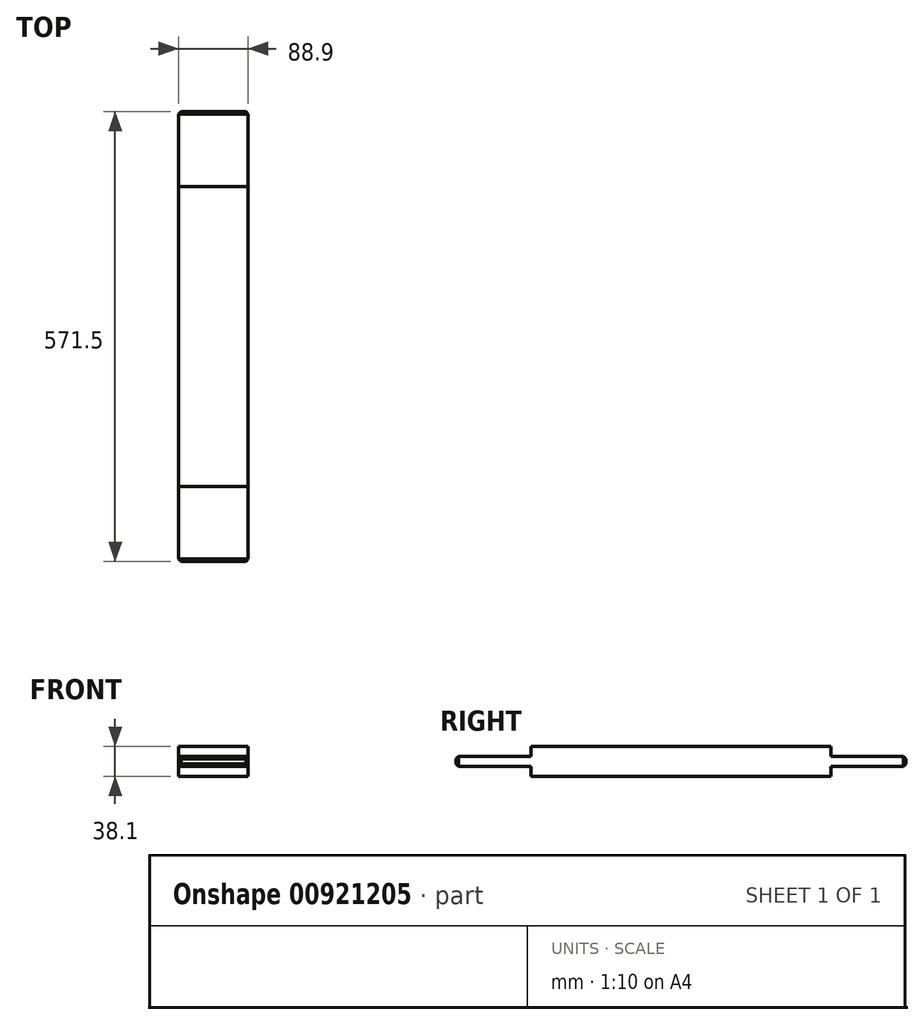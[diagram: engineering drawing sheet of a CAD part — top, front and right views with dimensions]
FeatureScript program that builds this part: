
annotation { "Feature Type Name" : "Feature", "Feature Type Description" : "" }
export const myFeature = defineFeature(function(context is Context, id is Id, definition is map)
    precondition{}
    {
        {
            var Q0;
            Q0=qCreatedBy(makeId("Front.planeOp"),FACE);
            var sketch = newSketch(context, id + "F0", { "sketchPlane" : qUnion([Q0])});
            skLineSegment(sketch, "E0.bottom", {"start": v(0, 0) * mm, "end": v(88.9, 0) * mm});
            skLineSegment(sketch, "E0.top", {"start": v(0, 38.1) * mm, "end": v(88.9, 38.1) * mm});
            skLineSegment(sketch, "E0.left", {"start": v(0, 0) * mm, "end": v(0, 38.1) * mm});
            skLineSegment(sketch, "E0.right", {"start": v(88.9, 0) * mm, "end": v(88.9, 38.1) * mm});
            skSolve(sketch);
        }
        {
            var Q0;
            Q0 = qSketchRegion(id + "F0", true);
            extrude(context, id + "F1", {"entities" : qUnion([Q0]), "depth" : 190.5 * mm, "offsetDistance" : 25.4 * mm});
        }
        {
            var Q0;
            Q0=makeQuery(id+"F1.opExtrude","CAP_FACE",FACE,{"disambiguationData":[OSD([sQuery(id+"F0.wireOp",EDGE,"E0.bottom"),sQuery(id+"F0.wireOp",EDGE,"E0.top"),sQuery(id+"F0.wireOp",EDGE,"E0.left"),sQuery(id+"F0.wireOp",EDGE,"E0.right")])],"isStart":false});
            var sketch = newSketch(context, id + "F2", { "sketchPlane" : qUnion([Q0])});
            skLineSegment(sketch, "E1.bottom", {"start": v(88.9, 12.7) * mm, "end": v(0, 12.7) * mm});
            skLineSegment(sketch, "E1.top", {"start": v(88.9, 25.4) * mm, "end": v(0, 25.4) * mm});
            skLineSegment(sketch, "E1.left", {"start": v(88.9, 12.7) * mm, "end": v(88.9, 25.4) * mm});
            skLineSegment(sketch, "E1.right", {"start": v(0, 12.7) * mm, "end": v(0, 25.4) * mm});
            skSolve(sketch);
        }
        {
            var Q0;
            Q0 = qSketchRegion(id + "F2", true);
            extrude(context, id + "F3", {"entities" : qUnion([Q0]), "operationType" : NewBodyOperationType.ADD, "depth" : 95.25 * mm, "offsetDistance" : 25.4 * mm});
        }
        {
            var Q0;
            Q0=makeQuery(id+"F3.opExtrude","CAP_EDGE",EDGE,{"disambiguationData":[OSD([sQuery(id+"F2.wireOp",EDGE,"E1.top")])],"isStart":false});
            var Q1;
            Q1=makeQuery(id+"F3.opExtrude","CAP_EDGE",EDGE,{"disambiguationData":[OSD([sQuery(id+"F2.wireOp",EDGE,"E1.right")])],"isStart":false});
            var Q2;
            Q2=makeQuery(id+"F3.opExtrude","CAP_EDGE",EDGE,{"disambiguationData":[OSD([sQuery(id+"F2.wireOp",EDGE,"E1.bottom")])],"isStart":false});
            var Q3;
            Q3=makeQuery(id+"F3.opExtrude","CAP_EDGE",EDGE,{"disambiguationData":[OSD([sQuery(id+"F2.wireOp",EDGE,"E1.left")])],"isStart":false});
            chamfer(context, id + "F4", {"entities" : qUnion([Q0, Q1, Q2, Q3]), "width" : 3.17 * mm, "tangentPropagation" : true});
        }
        {
            var Q0;
            Q0=makeQuery(id+"F1.opExtrude","SWEPT_BODY",BODY,{"disambiguationData":[OSD([sQuery(id+"F0.wireOp",EDGE,"E0.bottom"),sQuery(id+"F0.wireOp",EDGE,"E0.top"),sQuery(id+"F0.wireOp",EDGE,"E0.left"),sQuery(id+"F0.wireOp",EDGE,"E0.right")])]});
            var Q1;
            Q1=makeQuery(id+"F1.opExtrude","CAP_FACE",FACE,{"disambiguationData":[OSD([sQuery(id+"F0.wireOp",EDGE,"E0.bottom"),sQuery(id+"F0.wireOp",EDGE,"E0.top"),sQuery(id+"F0.wireOp",EDGE,"E0.left"),sQuery(id+"F0.wireOp",EDGE,"E0.right")])],"isStart":true});
            mirror(context, id + "F5", {"operationType" : NewBodyOperationType.ADD, "entities" : qUnion([Q0]), "mirrorPlane" : qUnion([Q1])});
        }
    });
